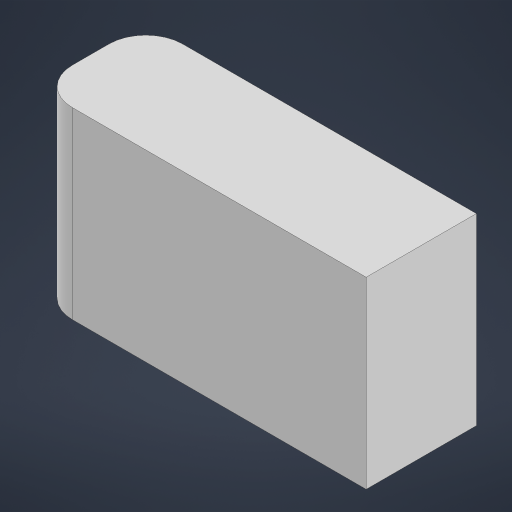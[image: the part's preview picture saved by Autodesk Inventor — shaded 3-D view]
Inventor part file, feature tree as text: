
AUTODESK INVENTOR PART (.ipt)
format: ipt  version: 2024 (Build 280153000, 153)  size: 136,192 bytes
history: native  units: mm
features: other x1, extrude x1, sketch x1
ambient origin geometry x8: Origin, YZ Plane, XZ Plane, XY Plane, X Axis, Y Axis, Z Axis, Center Point
bodies: Body1 (feature_tree)
feature tree (3):
  other  "Těleso1"
  extrude  "Vysunutí1"  Depth=15.0mm
  sketch  "Náčrt1"
